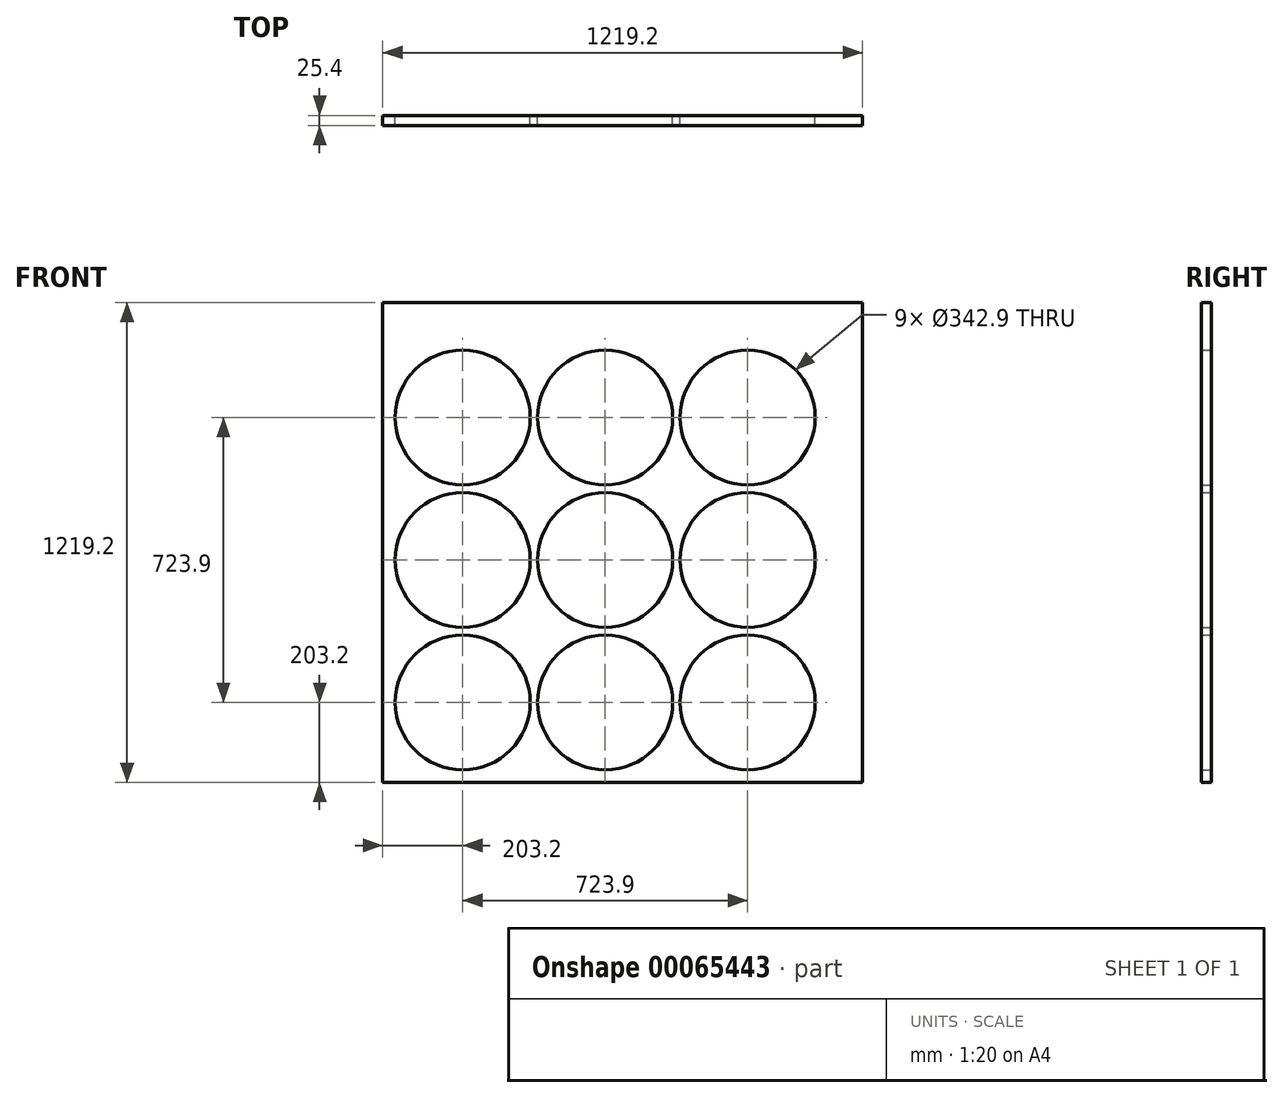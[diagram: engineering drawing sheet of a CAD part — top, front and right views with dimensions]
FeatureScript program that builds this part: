
annotation { "Feature Type Name" : "Feature", "Feature Type Description" : "" }
export const myFeature = defineFeature(function(context is Context, id is Id, definition is map)
    precondition{}
    {
        {
            var Q0;
            Q0=qCreatedBy(makeId("Front.planeOp"),FACE);
            var sketch = newSketch(context, id + "F0", { "sketchPlane" : qUnion([Q0])});
            skLineSegment(sketch, "E0", {"start": v(-609.6, 609.6) * mm, "end": v(-609.6, -609.6) * mm});
            skLineSegment(sketch, "E1", {"start": v(-609.6, -609.6) * mm, "end": v(609.6, -609.6) * mm});
            skLineSegment(sketch, "E2", {"start": v(609.6, -609.6) * mm, "end": v(609.6, 609.6) * mm});
            skLineSegment(sketch, "E3", {"start": v(609.6, 609.6) * mm, "end": v(-609.6, 609.6) * mm});
            skCircle(sketch, "E4", {"center": v(-406.4, -406.4) * mm, "radius": 171.45 * mm});
            skCircle(sketch, "E5", {"center": v(-406.4, -406.4) * mm, "radius": 69.85 * mm});
            skLineSegment(sketch, "E6", {"start": v(-387.25, -304.8) * mm, "end": v(-383, -282.22) * mm});
            skArc(sketch, "E7", {"start": v(-383, -282.22) * mm, "mid": v(-406.4, -254) * mm, "end": v(-429.8, -282.22) * mm});
            skLineSegment(sketch, "E8", {"start": v(-429.8, -282.22) * mm, "end": v(-425.55, -304.8) * mm});
            skArc(sketch, "E9", {"start": v(-425.55, -304.8) * mm, "mid": v(-406.4, -320.68) * mm, "end": v(-387.25, -304.8) * mm});
            skLineSegment(sketch, "E10", {"start": v(-440.62, -308.84) * mm, "end": v(-448.22, -287.16) * mm});
            skArc(sketch, "E11", {"start": v(-448.22, -287.16) * mm, "mid": v(-482.6, -274.42) * mm, "end": v(-488.75, -310.56) * mm});
            skLineSegment(sketch, "E12", {"start": v(-488.75, -310.56) * mm, "end": v(-473.78, -327.98) * mm});
            skArc(sketch, "E13", {"start": v(-473.78, -327.98) * mm, "mid": v(-449.26, -332.16) * mm, "end": v(-440.62, -308.84) * mm});
            skLineSegment(sketch, "E14", {"start": v(-484.82, -339.02) * mm, "end": v(-502.24, -324.05) * mm});
            skArc(sketch, "E15", {"start": v(-502.24, -324.05) * mm, "mid": v(-538.38, -330.2) * mm, "end": v(-525.64, -364.58) * mm});
            skLineSegment(sketch, "E16", {"start": v(-525.64, -364.58) * mm, "end": v(-503.96, -372.18) * mm});
            skArc(sketch, "E17", {"start": v(-503.96, -372.18) * mm, "mid": v(-480.64, -363.54) * mm, "end": v(-484.82, -339.02) * mm});
            skLineSegment(sketch, "E18", {"start": v(-508, -387.25) * mm, "end": v(-530.58, -383) * mm});
            skArc(sketch, "E19", {"start": v(-530.58, -383) * mm, "mid": v(-558.8, -406.4) * mm, "end": v(-530.58, -429.8) * mm});
            skLineSegment(sketch, "E20", {"start": v(-530.58, -429.8) * mm, "end": v(-508, -425.55) * mm});
            skArc(sketch, "E21", {"start": v(-508, -425.55) * mm, "mid": v(-492.13, -406.4) * mm, "end": v(-508, -387.25) * mm});
            skLineSegment(sketch, "E22", {"start": v(-503.96, -440.62) * mm, "end": v(-525.64, -448.22) * mm});
            skArc(sketch, "E23", {"start": v(-525.64, -448.22) * mm, "mid": v(-538.38, -482.6) * mm, "end": v(-502.24, -488.75) * mm});
            skLineSegment(sketch, "E24", {"start": v(-502.24, -488.75) * mm, "end": v(-484.82, -473.78) * mm});
            skArc(sketch, "E25", {"start": v(-484.82, -473.78) * mm, "mid": v(-480.64, -449.26) * mm, "end": v(-503.96, -440.62) * mm});
            skLineSegment(sketch, "E26", {"start": v(-473.78, -484.82) * mm, "end": v(-488.75, -502.24) * mm});
            skArc(sketch, "E27", {"start": v(-488.75, -502.24) * mm, "mid": v(-482.6, -538.38) * mm, "end": v(-448.22, -525.64) * mm});
            skLineSegment(sketch, "E28", {"start": v(-448.22, -525.64) * mm, "end": v(-440.62, -503.96) * mm});
            skArc(sketch, "E29", {"start": v(-440.62, -503.96) * mm, "mid": v(-449.26, -480.64) * mm, "end": v(-473.78, -484.82) * mm});
            skLineSegment(sketch, "E30", {"start": v(-425.55, -508) * mm, "end": v(-429.8, -530.58) * mm});
            skArc(sketch, "E31", {"start": v(-429.8, -530.58) * mm, "mid": v(-406.4, -558.8) * mm, "end": v(-383, -530.58) * mm});
            skLineSegment(sketch, "E32", {"start": v(-383, -530.58) * mm, "end": v(-387.25, -508) * mm});
            skArc(sketch, "E33", {"start": v(-387.25, -508) * mm, "mid": v(-406.4, -492.13) * mm, "end": v(-425.55, -508) * mm});
            skLineSegment(sketch, "E34", {"start": v(-372.18, -503.96) * mm, "end": v(-364.58, -525.64) * mm});
            skArc(sketch, "E35", {"start": v(-364.58, -525.64) * mm, "mid": v(-330.2, -538.38) * mm, "end": v(-324.05, -502.24) * mm});
            skLineSegment(sketch, "E36", {"start": v(-324.05, -502.24) * mm, "end": v(-339.02, -484.82) * mm});
            skArc(sketch, "E37", {"start": v(-339.02, -484.82) * mm, "mid": v(-363.54, -480.64) * mm, "end": v(-372.18, -503.96) * mm});
            skLineSegment(sketch, "E38", {"start": v(-327.98, -473.78) * mm, "end": v(-310.56, -488.75) * mm});
            skArc(sketch, "E39", {"start": v(-310.56, -488.75) * mm, "mid": v(-274.42, -482.6) * mm, "end": v(-287.16, -448.22) * mm});
            skLineSegment(sketch, "E40", {"start": v(-287.16, -448.22) * mm, "end": v(-308.84, -440.62) * mm});
            skArc(sketch, "E41", {"start": v(-308.84, -440.62) * mm, "mid": v(-332.16, -449.26) * mm, "end": v(-327.98, -473.78) * mm});
            skLineSegment(sketch, "E42", {"start": v(-304.8, -425.55) * mm, "end": v(-282.22, -429.8) * mm});
            skArc(sketch, "E43", {"start": v(-282.22, -429.8) * mm, "mid": v(-254, -406.4) * mm, "end": v(-282.22, -383) * mm});
            skLineSegment(sketch, "E44", {"start": v(-282.22, -383) * mm, "end": v(-304.8, -387.25) * mm});
            skArc(sketch, "E45", {"start": v(-304.8, -387.25) * mm, "mid": v(-320.68, -406.4) * mm, "end": v(-304.8, -425.55) * mm});
            skLineSegment(sketch, "E46", {"start": v(-308.84, -372.18) * mm, "end": v(-287.16, -364.58) * mm});
            skArc(sketch, "E47", {"start": v(-287.16, -364.58) * mm, "mid": v(-274.42, -330.2) * mm, "end": v(-310.56, -324.05) * mm});
            skLineSegment(sketch, "E48", {"start": v(-310.56, -324.05) * mm, "end": v(-327.98, -339.02) * mm});
            skArc(sketch, "E49", {"start": v(-327.98, -339.02) * mm, "mid": v(-332.16, -363.54) * mm, "end": v(-308.84, -372.18) * mm});
            skLineSegment(sketch, "E50", {"start": v(-339.02, -327.98) * mm, "end": v(-324.05, -310.56) * mm});
            skArc(sketch, "E51", {"start": v(-324.05, -310.56) * mm, "mid": v(-330.2, -274.42) * mm, "end": v(-364.58, -287.16) * mm});
            skLineSegment(sketch, "E52", {"start": v(-364.58, -287.16) * mm, "end": v(-372.18, -308.84) * mm});
            skArc(sketch, "E53", {"start": v(-372.18, -308.84) * mm, "mid": v(-363.54, -332.16) * mm, "end": v(-339.02, -327.98) * mm});
            skCircle(sketch, "E54", {"center": v(-445.73, -259.64) * mm, "radius": 7.94 * mm});
            skCircle(sketch, "E55", {"center": v(-513.84, -298.96) * mm, "radius": 7.94 * mm});
            skCircle(sketch, "E56", {"center": v(-553.16, -367.07) * mm, "radius": 7.94 * mm});
            skCircle(sketch, "E57", {"center": v(-553.16, -445.73) * mm, "radius": 7.94 * mm});
            skCircle(sketch, "E58", {"center": v(-513.84, -513.84) * mm, "radius": 7.94 * mm});
            skCircle(sketch, "E59", {"center": v(-445.73, -553.16) * mm, "radius": 7.94 * mm});
            skCircle(sketch, "E60", {"center": v(-367.07, -553.16) * mm, "radius": 7.94 * mm});
            skCircle(sketch, "E61", {"center": v(-298.96, -513.84) * mm, "radius": 7.94 * mm});
            skCircle(sketch, "E62", {"center": v(-259.64, -445.73) * mm, "radius": 7.94 * mm});
            skCircle(sketch, "E63", {"center": v(-259.64, -367.07) * mm, "radius": 7.94 * mm});
            skCircle(sketch, "E64", {"center": v(-298.96, -298.96) * mm, "radius": 7.94 * mm});
            skCircle(sketch, "E65", {"center": v(-367.07, -259.64) * mm, "radius": 7.94 * mm});
            skCircle(sketch, "E66", {"center": v(-44.45, -406.4) * mm, "radius": 171.45 * mm});
            skCircle(sketch, "E67", {"center": v(-44.45, -406.4) * mm, "radius": 69.85 * mm});
            skLineSegment(sketch, "E68", {"start": v(-25.3, -304.8) * mm, "end": v(-21.05, -282.22) * mm});
            skArc(sketch, "E69", {"start": v(-21.05, -282.22) * mm, "mid": v(-44.45, -254) * mm, "end": v(-67.85, -282.22) * mm});
            skLineSegment(sketch, "E70", {"start": v(-67.85, -282.22) * mm, "end": v(-63.6, -304.8) * mm});
            skArc(sketch, "E71", {"start": v(-63.6, -304.8) * mm, "mid": v(-44.45, -320.68) * mm, "end": v(-25.3, -304.8) * mm});
            skLineSegment(sketch, "E72", {"start": v(-78.67, -308.84) * mm, "end": v(-86.27, -287.16) * mm});
            skArc(sketch, "E73", {"start": v(-86.27, -287.16) * mm, "mid": v(-120.65, -274.42) * mm, "end": v(-126.8, -310.56) * mm});
            skLineSegment(sketch, "E74", {"start": v(-126.8, -310.56) * mm, "end": v(-111.83, -327.98) * mm});
            skArc(sketch, "E75", {"start": v(-111.83, -327.98) * mm, "mid": v(-87.31, -332.16) * mm, "end": v(-78.67, -308.84) * mm});
            skLineSegment(sketch, "E76", {"start": v(-122.87, -339.02) * mm, "end": v(-140.3, -324.05) * mm});
            skArc(sketch, "E77", {"start": v(-140.3, -324.05) * mm, "mid": v(-176.43, -330.2) * mm, "end": v(-163.7, -364.58) * mm});
            skLineSegment(sketch, "E78", {"start": v(-163.7, -364.58) * mm, "end": v(-142.01, -372.18) * mm});
            skArc(sketch, "E79", {"start": v(-142.01, -372.18) * mm, "mid": v(-118.7, -363.54) * mm, "end": v(-122.87, -339.02) * mm});
            skLineSegment(sketch, "E80", {"start": v(-146.05, -387.25) * mm, "end": v(-168.63, -383) * mm});
            skArc(sketch, "E81", {"start": v(-168.63, -383) * mm, "mid": v(-196.85, -406.4) * mm, "end": v(-168.63, -429.8) * mm});
            skLineSegment(sketch, "E82", {"start": v(-168.63, -429.8) * mm, "end": v(-146.05, -425.55) * mm});
            skArc(sketch, "E83", {"start": v(-146.05, -425.55) * mm, "mid": v(-130.18, -406.4) * mm, "end": v(-146.05, -387.25) * mm});
            skLineSegment(sketch, "E84", {"start": v(-142.01, -440.62) * mm, "end": v(-163.7, -448.22) * mm});
            skArc(sketch, "E85", {"start": v(-163.7, -448.22) * mm, "mid": v(-176.43, -482.6) * mm, "end": v(-140.3, -488.75) * mm});
            skLineSegment(sketch, "E86", {"start": v(-140.3, -488.75) * mm, "end": v(-122.87, -473.78) * mm});
            skArc(sketch, "E87", {"start": v(-122.87, -473.78) * mm, "mid": v(-118.7, -449.26) * mm, "end": v(-142.01, -440.62) * mm});
            skLineSegment(sketch, "E88", {"start": v(-111.83, -484.82) * mm, "end": v(-126.8, -502.24) * mm});
            skArc(sketch, "E89", {"start": v(-126.8, -502.24) * mm, "mid": v(-120.65, -538.38) * mm, "end": v(-86.27, -525.64) * mm});
            skLineSegment(sketch, "E90", {"start": v(-86.27, -525.64) * mm, "end": v(-78.67, -503.96) * mm});
            skArc(sketch, "E91", {"start": v(-78.67, -503.96) * mm, "mid": v(-87.31, -480.64) * mm, "end": v(-111.83, -484.82) * mm});
            skLineSegment(sketch, "E92", {"start": v(-63.6, -508) * mm, "end": v(-67.85, -530.58) * mm});
            skArc(sketch, "E93", {"start": v(-67.85, -530.58) * mm, "mid": v(-44.45, -558.8) * mm, "end": v(-21.05, -530.58) * mm});
            skLineSegment(sketch, "E94", {"start": v(-21.05, -530.58) * mm, "end": v(-25.3, -508) * mm});
            skArc(sketch, "E95", {"start": v(-25.3, -508) * mm, "mid": v(-44.45, -492.13) * mm, "end": v(-63.6, -508) * mm});
            skLineSegment(sketch, "E96", {"start": v(-10.23, -503.96) * mm, "end": v(-2.63, -525.64) * mm});
            skArc(sketch, "E97", {"start": v(-2.63, -525.64) * mm, "mid": v(31.75, -538.38) * mm, "end": v(37.9, -502.24) * mm});
            skLineSegment(sketch, "E98", {"start": v(37.9, -502.24) * mm, "end": v(22.93, -484.82) * mm});
            skArc(sketch, "E99", {"start": v(22.93, -484.82) * mm, "mid": v(-1.59, -480.64) * mm, "end": v(-10.23, -503.96) * mm});
            skLineSegment(sketch, "E100", {"start": v(33.97, -473.78) * mm, "end": v(51.4, -488.75) * mm});
            skArc(sketch, "E101", {"start": v(51.4, -488.75) * mm, "mid": v(87.53, -482.6) * mm, "end": v(74.8, -448.22) * mm});
            skLineSegment(sketch, "E102", {"start": v(74.8, -448.22) * mm, "end": v(53.11, -440.62) * mm});
            skArc(sketch, "E103", {"start": v(53.11, -440.62) * mm, "mid": v(29.8, -449.26) * mm, "end": v(33.97, -473.78) * mm});
            skLineSegment(sketch, "E104", {"start": v(57.15, -425.55) * mm, "end": v(79.73, -429.8) * mm});
            skArc(sketch, "E105", {"start": v(79.73, -429.8) * mm, "mid": v(107.95, -406.4) * mm, "end": v(79.73, -383) * mm});
            skLineSegment(sketch, "E106", {"start": v(79.73, -383) * mm, "end": v(57.15, -387.25) * mm});
            skArc(sketch, "E107", {"start": v(57.15, -387.25) * mm, "mid": v(41.27, -406.4) * mm, "end": v(57.15, -425.55) * mm});
            skLineSegment(sketch, "E108", {"start": v(53.11, -372.18) * mm, "end": v(74.8, -364.58) * mm});
            skArc(sketch, "E109", {"start": v(74.8, -364.58) * mm, "mid": v(87.53, -330.2) * mm, "end": v(51.4, -324.05) * mm});
            skLineSegment(sketch, "E110", {"start": v(51.4, -324.05) * mm, "end": v(33.97, -339.02) * mm});
            skArc(sketch, "E111", {"start": v(33.97, -339.02) * mm, "mid": v(29.8, -363.54) * mm, "end": v(53.11, -372.18) * mm});
            skLineSegment(sketch, "E112", {"start": v(22.93, -327.98) * mm, "end": v(37.9, -310.56) * mm});
            skArc(sketch, "E113", {"start": v(37.9, -310.56) * mm, "mid": v(31.75, -274.42) * mm, "end": v(-2.63, -287.16) * mm});
            skLineSegment(sketch, "E114", {"start": v(-2.63, -287.16) * mm, "end": v(-10.23, -308.84) * mm});
            skArc(sketch, "E115", {"start": v(-10.23, -308.84) * mm, "mid": v(-1.59, -332.16) * mm, "end": v(22.93, -327.98) * mm});
            skCircle(sketch, "E116", {"center": v(-83.78, -259.64) * mm, "radius": 7.94 * mm});
            skCircle(sketch, "E117", {"center": v(-151.89, -298.96) * mm, "radius": 7.94 * mm});
            skCircle(sketch, "E118", {"center": v(-191.21, -367.07) * mm, "radius": 7.94 * mm});
            skCircle(sketch, "E119", {"center": v(-191.21, -445.73) * mm, "radius": 7.94 * mm});
            skCircle(sketch, "E120", {"center": v(-151.89, -513.84) * mm, "radius": 7.94 * mm});
            skCircle(sketch, "E121", {"center": v(-83.78, -553.16) * mm, "radius": 7.94 * mm});
            skCircle(sketch, "E122", {"center": v(-5.12, -553.16) * mm, "radius": 7.94 * mm});
            skCircle(sketch, "E123", {"center": v(62.99, -513.84) * mm, "radius": 7.94 * mm});
            skCircle(sketch, "E124", {"center": v(102.31, -445.73) * mm, "radius": 7.94 * mm});
            skCircle(sketch, "E125", {"center": v(102.31, -367.07) * mm, "radius": 7.94 * mm});
            skCircle(sketch, "E126", {"center": v(62.99, -298.96) * mm, "radius": 7.94 * mm});
            skCircle(sketch, "E127", {"center": v(-5.12, -259.64) * mm, "radius": 7.94 * mm});
            skCircle(sketch, "E128", {"center": v(317.5, -406.4) * mm, "radius": 171.45 * mm});
            skCircle(sketch, "E129", {"center": v(317.5, -406.4) * mm, "radius": 69.85 * mm});
            skLineSegment(sketch, "E130", {"start": v(336.65, -304.8) * mm, "end": v(340.9, -282.22) * mm});
            skArc(sketch, "E131", {"start": v(340.9, -282.22) * mm, "mid": v(317.5, -254) * mm, "end": v(294.1, -282.22) * mm});
            skLineSegment(sketch, "E132", {"start": v(294.1, -282.22) * mm, "end": v(298.35, -304.8) * mm});
            skArc(sketch, "E133", {"start": v(298.35, -304.8) * mm, "mid": v(317.5, -320.68) * mm, "end": v(336.65, -304.8) * mm});
            skLineSegment(sketch, "E134", {"start": v(283.28, -308.84) * mm, "end": v(275.68, -287.16) * mm});
            skArc(sketch, "E135", {"start": v(275.68, -287.16) * mm, "mid": v(241.3, -274.42) * mm, "end": v(235.15, -310.56) * mm});
            skLineSegment(sketch, "E136", {"start": v(235.15, -310.56) * mm, "end": v(250.12, -327.98) * mm});
            skArc(sketch, "E137", {"start": v(250.12, -327.98) * mm, "mid": v(274.64, -332.16) * mm, "end": v(283.28, -308.84) * mm});
            skLineSegment(sketch, "E138", {"start": v(239.08, -339.02) * mm, "end": v(221.66, -324.05) * mm});
            skArc(sketch, "E139", {"start": v(221.66, -324.05) * mm, "mid": v(185.52, -330.2) * mm, "end": v(198.26, -364.58) * mm});
            skLineSegment(sketch, "E140", {"start": v(198.26, -364.58) * mm, "end": v(219.94, -372.18) * mm});
            skArc(sketch, "E141", {"start": v(219.94, -372.18) * mm, "mid": v(243.26, -363.54) * mm, "end": v(239.08, -339.02) * mm});
            skLineSegment(sketch, "E142", {"start": v(215.9, -387.25) * mm, "end": v(193.32, -383) * mm});
            skArc(sketch, "E143", {"start": v(193.32, -383) * mm, "mid": v(165.1, -406.4) * mm, "end": v(193.32, -429.8) * mm});
            skLineSegment(sketch, "E144", {"start": v(193.32, -429.8) * mm, "end": v(215.9, -425.55) * mm});
            skArc(sketch, "E145", {"start": v(215.9, -425.55) * mm, "mid": v(231.77, -406.4) * mm, "end": v(215.9, -387.25) * mm});
            skLineSegment(sketch, "E146", {"start": v(219.94, -440.62) * mm, "end": v(198.26, -448.22) * mm});
            skArc(sketch, "E147", {"start": v(198.26, -448.22) * mm, "mid": v(185.52, -482.6) * mm, "end": v(221.66, -488.75) * mm});
            skLineSegment(sketch, "E148", {"start": v(221.66, -488.75) * mm, "end": v(239.08, -473.78) * mm});
            skArc(sketch, "E149", {"start": v(239.08, -473.78) * mm, "mid": v(243.26, -449.26) * mm, "end": v(219.94, -440.62) * mm});
            skLineSegment(sketch, "E150", {"start": v(250.12, -484.82) * mm, "end": v(235.15, -502.24) * mm});
            skArc(sketch, "E151", {"start": v(235.15, -502.24) * mm, "mid": v(241.3, -538.38) * mm, "end": v(275.68, -525.64) * mm});
            skLineSegment(sketch, "E152", {"start": v(275.68, -525.64) * mm, "end": v(283.28, -503.96) * mm});
            skArc(sketch, "E153", {"start": v(283.28, -503.96) * mm, "mid": v(274.64, -480.64) * mm, "end": v(250.12, -484.82) * mm});
            skLineSegment(sketch, "E154", {"start": v(298.35, -508) * mm, "end": v(294.1, -530.58) * mm});
            skArc(sketch, "E155", {"start": v(294.1, -530.58) * mm, "mid": v(317.5, -558.8) * mm, "end": v(340.9, -530.58) * mm});
            skLineSegment(sketch, "E156", {"start": v(340.9, -530.58) * mm, "end": v(336.65, -508) * mm});
            skArc(sketch, "E157", {"start": v(336.65, -508) * mm, "mid": v(317.5, -492.13) * mm, "end": v(298.35, -508) * mm});
            skLineSegment(sketch, "E158", {"start": v(351.72, -503.96) * mm, "end": v(359.32, -525.64) * mm});
            skArc(sketch, "E159", {"start": v(359.32, -525.64) * mm, "mid": v(393.7, -538.38) * mm, "end": v(399.85, -502.24) * mm});
            skLineSegment(sketch, "E160", {"start": v(399.85, -502.24) * mm, "end": v(384.88, -484.82) * mm});
            skArc(sketch, "E161", {"start": v(384.88, -484.82) * mm, "mid": v(360.36, -480.64) * mm, "end": v(351.72, -503.96) * mm});
            skLineSegment(sketch, "E162", {"start": v(395.92, -473.78) * mm, "end": v(413.34, -488.75) * mm});
            skArc(sketch, "E163", {"start": v(413.34, -488.75) * mm, "mid": v(449.48, -482.6) * mm, "end": v(436.74, -448.22) * mm});
            skLineSegment(sketch, "E164", {"start": v(436.74, -448.22) * mm, "end": v(415.06, -440.62) * mm});
            skArc(sketch, "E165", {"start": v(415.06, -440.62) * mm, "mid": v(391.74, -449.26) * mm, "end": v(395.92, -473.78) * mm});
            skLineSegment(sketch, "E166", {"start": v(419.1, -425.55) * mm, "end": v(441.68, -429.8) * mm});
            skArc(sketch, "E167", {"start": v(441.68, -429.8) * mm, "mid": v(469.9, -406.4) * mm, "end": v(441.68, -383) * mm});
            skLineSegment(sketch, "E168", {"start": v(441.68, -383) * mm, "end": v(419.1, -387.25) * mm});
            skArc(sketch, "E169", {"start": v(419.1, -387.25) * mm, "mid": v(403.23, -406.4) * mm, "end": v(419.1, -425.55) * mm});
            skLineSegment(sketch, "E170", {"start": v(415.06, -372.18) * mm, "end": v(436.74, -364.58) * mm});
            skArc(sketch, "E171", {"start": v(436.74, -364.58) * mm, "mid": v(449.48, -330.2) * mm, "end": v(413.34, -324.05) * mm});
            skLineSegment(sketch, "E172", {"start": v(413.34, -324.05) * mm, "end": v(395.92, -339.02) * mm});
            skArc(sketch, "E173", {"start": v(395.92, -339.02) * mm, "mid": v(391.74, -363.54) * mm, "end": v(415.06, -372.18) * mm});
            skLineSegment(sketch, "E174", {"start": v(384.88, -327.98) * mm, "end": v(399.85, -310.56) * mm});
            skArc(sketch, "E175", {"start": v(399.85, -310.56) * mm, "mid": v(393.7, -274.42) * mm, "end": v(359.32, -287.16) * mm});
            skLineSegment(sketch, "E176", {"start": v(359.32, -287.16) * mm, "end": v(351.72, -308.84) * mm});
            skArc(sketch, "E177", {"start": v(351.72, -308.84) * mm, "mid": v(360.36, -332.16) * mm, "end": v(384.88, -327.98) * mm});
            skCircle(sketch, "E178", {"center": v(278.17, -259.64) * mm, "radius": 7.94 * mm});
            skCircle(sketch, "E179", {"center": v(210.06, -298.96) * mm, "radius": 7.94 * mm});
            skCircle(sketch, "E180", {"center": v(170.74, -367.07) * mm, "radius": 7.94 * mm});
            skCircle(sketch, "E181", {"center": v(170.74, -445.73) * mm, "radius": 7.94 * mm});
            skCircle(sketch, "E182", {"center": v(210.06, -513.84) * mm, "radius": 7.94 * mm});
            skCircle(sketch, "E183", {"center": v(278.17, -553.16) * mm, "radius": 7.94 * mm});
            skCircle(sketch, "E184", {"center": v(356.83, -553.16) * mm, "radius": 7.94 * mm});
            skCircle(sketch, "E185", {"center": v(424.94, -513.84) * mm, "radius": 7.94 * mm});
            skCircle(sketch, "E186", {"center": v(464.26, -445.73) * mm, "radius": 7.94 * mm});
            skCircle(sketch, "E187", {"center": v(464.26, -367.07) * mm, "radius": 7.94 * mm});
            skCircle(sketch, "E188", {"center": v(424.94, -298.96) * mm, "radius": 7.94 * mm});
            skCircle(sketch, "E189", {"center": v(356.83, -259.64) * mm, "radius": 7.94 * mm});
            skCircle(sketch, "E190", {"center": v(-44.45, -44.45) * mm, "radius": 171.45 * mm});
            skCircle(sketch, "E191", {"center": v(-44.45, -44.45) * mm, "radius": 69.85 * mm});
            skLineSegment(sketch, "E192", {"start": v(-25.3, 57.15) * mm, "end": v(-21.05, 79.73) * mm});
            skArc(sketch, "E193", {"start": v(-21.05, 79.73) * mm, "mid": v(-44.45, 107.95) * mm, "end": v(-67.85, 79.73) * mm});
            skLineSegment(sketch, "E194", {"start": v(-67.85, 79.73) * mm, "end": v(-63.6, 57.15) * mm});
            skArc(sketch, "E195", {"start": v(-63.6, 57.15) * mm, "mid": v(-44.45, 41.27) * mm, "end": v(-25.3, 57.15) * mm});
            skLineSegment(sketch, "E196", {"start": v(-78.67, 53.11) * mm, "end": v(-86.27, 74.8) * mm});
            skArc(sketch, "E197", {"start": v(-86.27, 74.8) * mm, "mid": v(-120.65, 87.53) * mm, "end": v(-126.8, 51.4) * mm});
            skLineSegment(sketch, "E198", {"start": v(-126.8, 51.4) * mm, "end": v(-111.83, 33.97) * mm});
            skArc(sketch, "E199", {"start": v(-111.83, 33.97) * mm, "mid": v(-87.31, 29.8) * mm, "end": v(-78.67, 53.11) * mm});
            skLineSegment(sketch, "E200", {"start": v(-122.87, 22.93) * mm, "end": v(-140.3, 37.9) * mm});
            skArc(sketch, "E201", {"start": v(-140.3, 37.9) * mm, "mid": v(-176.43, 31.75) * mm, "end": v(-163.7, -2.63) * mm});
            skLineSegment(sketch, "E202", {"start": v(-163.7, -2.63) * mm, "end": v(-142.01, -10.23) * mm});
            skArc(sketch, "E203", {"start": v(-142.01, -10.23) * mm, "mid": v(-118.7, -1.59) * mm, "end": v(-122.87, 22.93) * mm});
            skLineSegment(sketch, "E204", {"start": v(-146.05, -25.3) * mm, "end": v(-168.63, -21.05) * mm});
            skArc(sketch, "E205", {"start": v(-168.63, -21.05) * mm, "mid": v(-196.85, -44.45) * mm, "end": v(-168.63, -67.85) * mm});
            skLineSegment(sketch, "E206", {"start": v(-168.63, -67.85) * mm, "end": v(-146.05, -63.6) * mm});
            skArc(sketch, "E207", {"start": v(-146.05, -63.6) * mm, "mid": v(-130.18, -44.45) * mm, "end": v(-146.05, -25.3) * mm});
            skLineSegment(sketch, "E208", {"start": v(-142.01, -78.67) * mm, "end": v(-163.7, -86.27) * mm});
            skArc(sketch, "E209", {"start": v(-163.7, -86.27) * mm, "mid": v(-176.43, -120.65) * mm, "end": v(-140.3, -126.8) * mm});
            skLineSegment(sketch, "E210", {"start": v(-140.3, -126.8) * mm, "end": v(-122.87, -111.83) * mm});
            skArc(sketch, "E211", {"start": v(-122.87, -111.83) * mm, "mid": v(-118.7, -87.31) * mm, "end": v(-142.01, -78.67) * mm});
            skLineSegment(sketch, "E212", {"start": v(-111.83, -122.87) * mm, "end": v(-126.8, -140.3) * mm});
            skArc(sketch, "E213", {"start": v(-126.8, -140.3) * mm, "mid": v(-120.65, -176.43) * mm, "end": v(-86.27, -163.7) * mm});
            skLineSegment(sketch, "E214", {"start": v(-86.27, -163.7) * mm, "end": v(-78.67, -142.01) * mm});
            skArc(sketch, "E215", {"start": v(-78.67, -142.01) * mm, "mid": v(-87.31, -118.7) * mm, "end": v(-111.83, -122.87) * mm});
            skLineSegment(sketch, "E216", {"start": v(-63.6, -146.05) * mm, "end": v(-67.85, -168.63) * mm});
            skArc(sketch, "E217", {"start": v(-67.85, -168.63) * mm, "mid": v(-44.45, -196.85) * mm, "end": v(-21.05, -168.63) * mm});
            skLineSegment(sketch, "E218", {"start": v(-21.05, -168.63) * mm, "end": v(-25.3, -146.05) * mm});
            skArc(sketch, "E219", {"start": v(-25.3, -146.05) * mm, "mid": v(-44.45, -130.18) * mm, "end": v(-63.6, -146.05) * mm});
            skLineSegment(sketch, "E220", {"start": v(-10.23, -142.01) * mm, "end": v(-2.63, -163.7) * mm});
            skArc(sketch, "E221", {"start": v(-2.63, -163.7) * mm, "mid": v(31.75, -176.43) * mm, "end": v(37.9, -140.3) * mm});
            skLineSegment(sketch, "E222", {"start": v(37.9, -140.3) * mm, "end": v(22.93, -122.87) * mm});
            skArc(sketch, "E223", {"start": v(22.93, -122.87) * mm, "mid": v(-1.59, -118.7) * mm, "end": v(-10.23, -142.01) * mm});
            skLineSegment(sketch, "E224", {"start": v(33.97, -111.83) * mm, "end": v(51.4, -126.8) * mm});
            skArc(sketch, "E225", {"start": v(51.4, -126.8) * mm, "mid": v(87.53, -120.65) * mm, "end": v(74.8, -86.27) * mm});
            skLineSegment(sketch, "E226", {"start": v(74.8, -86.27) * mm, "end": v(53.11, -78.67) * mm});
            skArc(sketch, "E227", {"start": v(53.11, -78.67) * mm, "mid": v(29.8, -87.31) * mm, "end": v(33.97, -111.83) * mm});
            skLineSegment(sketch, "E228", {"start": v(57.15, -63.6) * mm, "end": v(79.73, -67.85) * mm});
            skArc(sketch, "E229", {"start": v(79.73, -67.85) * mm, "mid": v(107.95, -44.45) * mm, "end": v(79.73, -21.05) * mm});
            skLineSegment(sketch, "E230", {"start": v(79.73, -21.05) * mm, "end": v(57.15, -25.3) * mm});
            skArc(sketch, "E231", {"start": v(57.15, -25.3) * mm, "mid": v(41.27, -44.45) * mm, "end": v(57.15, -63.6) * mm});
            skLineSegment(sketch, "E232", {"start": v(53.11, -10.23) * mm, "end": v(74.8, -2.63) * mm});
            skArc(sketch, "E233", {"start": v(74.8, -2.63) * mm, "mid": v(87.53, 31.75) * mm, "end": v(51.4, 37.9) * mm});
            skLineSegment(sketch, "E234", {"start": v(51.4, 37.9) * mm, "end": v(33.97, 22.93) * mm});
            skArc(sketch, "E235", {"start": v(33.97, 22.93) * mm, "mid": v(29.8, -1.59) * mm, "end": v(53.11, -10.23) * mm});
            skLineSegment(sketch, "E236", {"start": v(22.93, 33.97) * mm, "end": v(37.9, 51.4) * mm});
            skArc(sketch, "E237", {"start": v(37.9, 51.4) * mm, "mid": v(31.75, 87.53) * mm, "end": v(-2.63, 74.8) * mm});
            skLineSegment(sketch, "E238", {"start": v(-2.63, 74.8) * mm, "end": v(-10.23, 53.11) * mm});
            skArc(sketch, "E239", {"start": v(-10.23, 53.11) * mm, "mid": v(-1.59, 29.8) * mm, "end": v(22.93, 33.97) * mm});
            skCircle(sketch, "E240", {"center": v(-83.78, 102.31) * mm, "radius": 7.94 * mm});
            skCircle(sketch, "E241", {"center": v(-151.89, 62.99) * mm, "radius": 7.94 * mm});
            skCircle(sketch, "E242", {"center": v(-191.21, -5.12) * mm, "radius": 7.94 * mm});
            skCircle(sketch, "E243", {"center": v(-191.21, -83.78) * mm, "radius": 7.94 * mm});
            skCircle(sketch, "E244", {"center": v(-151.89, -151.89) * mm, "radius": 7.94 * mm});
            skCircle(sketch, "E245", {"center": v(-83.78, -191.21) * mm, "radius": 7.94 * mm});
            skCircle(sketch, "E246", {"center": v(-5.12, -191.21) * mm, "radius": 7.94 * mm});
            skCircle(sketch, "E247", {"center": v(62.99, -151.89) * mm, "radius": 7.94 * mm});
            skCircle(sketch, "E248", {"center": v(102.31, -83.78) * mm, "radius": 7.94 * mm});
            skCircle(sketch, "E249", {"center": v(102.31, -5.12) * mm, "radius": 7.94 * mm});
            skCircle(sketch, "E250", {"center": v(62.99, 62.99) * mm, "radius": 7.94 * mm});
            skCircle(sketch, "E251", {"center": v(-5.12, 102.31) * mm, "radius": 7.94 * mm});
            skCircle(sketch, "E252", {"center": v(317.5, -44.45) * mm, "radius": 171.45 * mm});
            skCircle(sketch, "E253", {"center": v(317.5, -44.45) * mm, "radius": 69.85 * mm});
            skLineSegment(sketch, "E254", {"start": v(336.65, 57.15) * mm, "end": v(340.9, 79.73) * mm});
            skArc(sketch, "E255", {"start": v(340.9, 79.73) * mm, "mid": v(317.5, 107.95) * mm, "end": v(294.1, 79.73) * mm});
            skLineSegment(sketch, "E256", {"start": v(294.1, 79.73) * mm, "end": v(298.35, 57.15) * mm});
            skArc(sketch, "E257", {"start": v(298.35, 57.15) * mm, "mid": v(317.5, 41.27) * mm, "end": v(336.65, 57.15) * mm});
            skLineSegment(sketch, "E258", {"start": v(283.28, 53.11) * mm, "end": v(275.68, 74.8) * mm});
            skArc(sketch, "E259", {"start": v(275.68, 74.8) * mm, "mid": v(241.3, 87.53) * mm, "end": v(235.15, 51.4) * mm});
            skLineSegment(sketch, "E260", {"start": v(235.15, 51.4) * mm, "end": v(250.12, 33.97) * mm});
            skArc(sketch, "E261", {"start": v(250.12, 33.97) * mm, "mid": v(274.64, 29.8) * mm, "end": v(283.28, 53.11) * mm});
            skLineSegment(sketch, "E262", {"start": v(239.08, 22.93) * mm, "end": v(221.66, 37.9) * mm});
            skArc(sketch, "E263", {"start": v(221.66, 37.9) * mm, "mid": v(185.52, 31.75) * mm, "end": v(198.26, -2.63) * mm});
            skLineSegment(sketch, "E264", {"start": v(198.26, -2.63) * mm, "end": v(219.94, -10.23) * mm});
            skArc(sketch, "E265", {"start": v(219.94, -10.23) * mm, "mid": v(243.26, -1.59) * mm, "end": v(239.08, 22.93) * mm});
            skLineSegment(sketch, "E266", {"start": v(215.9, -25.3) * mm, "end": v(193.32, -21.05) * mm});
            skArc(sketch, "E267", {"start": v(193.32, -21.05) * mm, "mid": v(165.1, -44.45) * mm, "end": v(193.32, -67.85) * mm});
            skLineSegment(sketch, "E268", {"start": v(193.32, -67.85) * mm, "end": v(215.9, -63.6) * mm});
            skArc(sketch, "E269", {"start": v(215.9, -63.6) * mm, "mid": v(231.77, -44.45) * mm, "end": v(215.9, -25.3) * mm});
            skLineSegment(sketch, "E270", {"start": v(219.94, -78.67) * mm, "end": v(198.26, -86.27) * mm});
            skArc(sketch, "E271", {"start": v(198.26, -86.27) * mm, "mid": v(185.52, -120.65) * mm, "end": v(221.66, -126.8) * mm});
            skLineSegment(sketch, "E272", {"start": v(221.66, -126.8) * mm, "end": v(239.08, -111.83) * mm});
            skArc(sketch, "E273", {"start": v(239.08, -111.83) * mm, "mid": v(243.26, -87.31) * mm, "end": v(219.94, -78.67) * mm});
            skLineSegment(sketch, "E274", {"start": v(250.12, -122.87) * mm, "end": v(235.15, -140.3) * mm});
            skArc(sketch, "E275", {"start": v(235.15, -140.3) * mm, "mid": v(241.3, -176.43) * mm, "end": v(275.68, -163.7) * mm});
            skLineSegment(sketch, "E276", {"start": v(275.68, -163.7) * mm, "end": v(283.28, -142.01) * mm});
            skArc(sketch, "E277", {"start": v(283.28, -142.01) * mm, "mid": v(274.64, -118.7) * mm, "end": v(250.12, -122.87) * mm});
            skLineSegment(sketch, "E278", {"start": v(298.35, -146.05) * mm, "end": v(294.1, -168.63) * mm});
            skArc(sketch, "E279", {"start": v(294.1, -168.63) * mm, "mid": v(317.5, -196.85) * mm, "end": v(340.9, -168.63) * mm});
            skLineSegment(sketch, "E280", {"start": v(340.9, -168.63) * mm, "end": v(336.65, -146.05) * mm});
            skArc(sketch, "E281", {"start": v(336.65, -146.05) * mm, "mid": v(317.5, -130.18) * mm, "end": v(298.35, -146.05) * mm});
            skLineSegment(sketch, "E282", {"start": v(351.72, -142.01) * mm, "end": v(359.32, -163.7) * mm});
            skArc(sketch, "E283", {"start": v(359.32, -163.7) * mm, "mid": v(393.7, -176.43) * mm, "end": v(399.85, -140.3) * mm});
            skLineSegment(sketch, "E284", {"start": v(399.85, -140.3) * mm, "end": v(384.88, -122.87) * mm});
            skArc(sketch, "E285", {"start": v(384.88, -122.87) * mm, "mid": v(360.36, -118.7) * mm, "end": v(351.72, -142.01) * mm});
            skLineSegment(sketch, "E286", {"start": v(395.92, -111.83) * mm, "end": v(413.34, -126.8) * mm});
            skArc(sketch, "E287", {"start": v(413.34, -126.8) * mm, "mid": v(449.48, -120.65) * mm, "end": v(436.74, -86.27) * mm});
            skLineSegment(sketch, "E288", {"start": v(436.74, -86.27) * mm, "end": v(415.06, -78.67) * mm});
            skArc(sketch, "E289", {"start": v(415.06, -78.67) * mm, "mid": v(391.74, -87.31) * mm, "end": v(395.92, -111.83) * mm});
            skLineSegment(sketch, "E290", {"start": v(419.1, -63.6) * mm, "end": v(441.68, -67.85) * mm});
            skArc(sketch, "E291", {"start": v(441.68, -67.85) * mm, "mid": v(469.9, -44.45) * mm, "end": v(441.68, -21.05) * mm});
            skLineSegment(sketch, "E292", {"start": v(441.68, -21.05) * mm, "end": v(419.1, -25.3) * mm});
            skArc(sketch, "E293", {"start": v(419.1, -25.3) * mm, "mid": v(403.23, -44.45) * mm, "end": v(419.1, -63.6) * mm});
            skLineSegment(sketch, "E294", {"start": v(415.06, -10.23) * mm, "end": v(436.74, -2.63) * mm});
            skArc(sketch, "E295", {"start": v(436.74, -2.63) * mm, "mid": v(449.48, 31.75) * mm, "end": v(413.34, 37.9) * mm});
            skLineSegment(sketch, "E296", {"start": v(413.34, 37.9) * mm, "end": v(395.92, 22.93) * mm});
            skArc(sketch, "E297", {"start": v(395.92, 22.93) * mm, "mid": v(391.74, -1.59) * mm, "end": v(415.06, -10.23) * mm});
            skLineSegment(sketch, "E298", {"start": v(384.88, 33.97) * mm, "end": v(399.85, 51.4) * mm});
            skArc(sketch, "E299", {"start": v(399.85, 51.4) * mm, "mid": v(393.7, 87.53) * mm, "end": v(359.32, 74.8) * mm});
            skLineSegment(sketch, "E300", {"start": v(359.32, 74.8) * mm, "end": v(351.72, 53.11) * mm});
            skArc(sketch, "E301", {"start": v(351.72, 53.11) * mm, "mid": v(360.36, 29.8) * mm, "end": v(384.88, 33.97) * mm});
            skCircle(sketch, "E302", {"center": v(278.17, 102.31) * mm, "radius": 7.94 * mm});
            skCircle(sketch, "E303", {"center": v(210.06, 62.99) * mm, "radius": 7.94 * mm});
            skCircle(sketch, "E304", {"center": v(170.74, -5.12) * mm, "radius": 7.94 * mm});
            skCircle(sketch, "E305", {"center": v(170.74, -83.78) * mm, "radius": 7.94 * mm});
            skCircle(sketch, "E306", {"center": v(210.06, -151.89) * mm, "radius": 7.94 * mm});
            skCircle(sketch, "E307", {"center": v(278.17, -191.21) * mm, "radius": 7.94 * mm});
            skCircle(sketch, "E308", {"center": v(356.83, -191.21) * mm, "radius": 7.94 * mm});
            skCircle(sketch, "E309", {"center": v(424.94, -151.89) * mm, "radius": 7.94 * mm});
            skCircle(sketch, "E310", {"center": v(464.26, -83.78) * mm, "radius": 7.94 * mm});
            skCircle(sketch, "E311", {"center": v(464.26, -5.12) * mm, "radius": 7.94 * mm});
            skCircle(sketch, "E312", {"center": v(424.94, 62.99) * mm, "radius": 7.94 * mm});
            skCircle(sketch, "E313", {"center": v(356.83, 102.31) * mm, "radius": 7.94 * mm});
            skCircle(sketch, "E314", {"center": v(-406.4, -44.45) * mm, "radius": 171.45 * mm});
            skCircle(sketch, "E315", {"center": v(-406.4, -44.45) * mm, "radius": 69.85 * mm});
            skLineSegment(sketch, "E316", {"start": v(-387.25, 57.15) * mm, "end": v(-383, 79.73) * mm});
            skArc(sketch, "E317", {"start": v(-383, 79.73) * mm, "mid": v(-406.4, 107.95) * mm, "end": v(-429.8, 79.73) * mm});
            skLineSegment(sketch, "E318", {"start": v(-429.8, 79.73) * mm, "end": v(-425.55, 57.15) * mm});
            skArc(sketch, "E319", {"start": v(-425.55, 57.15) * mm, "mid": v(-406.4, 41.27) * mm, "end": v(-387.25, 57.15) * mm});
            skLineSegment(sketch, "E320", {"start": v(-440.62, 53.11) * mm, "end": v(-448.22, 74.8) * mm});
            skArc(sketch, "E321", {"start": v(-448.22, 74.8) * mm, "mid": v(-482.6, 87.53) * mm, "end": v(-488.75, 51.4) * mm});
            skLineSegment(sketch, "E322", {"start": v(-488.75, 51.4) * mm, "end": v(-473.78, 33.97) * mm});
            skArc(sketch, "E323", {"start": v(-473.78, 33.97) * mm, "mid": v(-449.26, 29.8) * mm, "end": v(-440.62, 53.11) * mm});
            skLineSegment(sketch, "E324", {"start": v(-484.82, 22.93) * mm, "end": v(-502.24, 37.9) * mm});
            skArc(sketch, "E325", {"start": v(-502.24, 37.9) * mm, "mid": v(-538.38, 31.75) * mm, "end": v(-525.64, -2.63) * mm});
            skLineSegment(sketch, "E326", {"start": v(-525.64, -2.63) * mm, "end": v(-503.96, -10.23) * mm});
            skArc(sketch, "E327", {"start": v(-503.96, -10.23) * mm, "mid": v(-480.64, -1.59) * mm, "end": v(-484.82, 22.93) * mm});
            skLineSegment(sketch, "E328", {"start": v(-508, -25.3) * mm, "end": v(-530.58, -21.05) * mm});
            skArc(sketch, "E329", {"start": v(-530.58, -21.05) * mm, "mid": v(-558.8, -44.45) * mm, "end": v(-530.58, -67.85) * mm});
            skLineSegment(sketch, "E330", {"start": v(-530.58, -67.85) * mm, "end": v(-508, -63.6) * mm});
            skArc(sketch, "E331", {"start": v(-508, -63.6) * mm, "mid": v(-492.13, -44.45) * mm, "end": v(-508, -25.3) * mm});
            skLineSegment(sketch, "E332", {"start": v(-503.96, -78.67) * mm, "end": v(-525.64, -86.27) * mm});
            skArc(sketch, "E333", {"start": v(-525.64, -86.27) * mm, "mid": v(-538.38, -120.65) * mm, "end": v(-502.24, -126.8) * mm});
            skLineSegment(sketch, "E334", {"start": v(-502.24, -126.8) * mm, "end": v(-484.82, -111.83) * mm});
            skArc(sketch, "E335", {"start": v(-484.82, -111.83) * mm, "mid": v(-480.64, -87.31) * mm, "end": v(-503.96, -78.67) * mm});
            skLineSegment(sketch, "E336", {"start": v(-473.78, -122.87) * mm, "end": v(-488.75, -140.3) * mm});
            skArc(sketch, "E337", {"start": v(-488.75, -140.3) * mm, "mid": v(-482.6, -176.43) * mm, "end": v(-448.22, -163.7) * mm});
            skLineSegment(sketch, "E338", {"start": v(-448.22, -163.7) * mm, "end": v(-440.62, -142.01) * mm});
            skArc(sketch, "E339", {"start": v(-440.62, -142.01) * mm, "mid": v(-449.26, -118.7) * mm, "end": v(-473.78, -122.87) * mm});
            skLineSegment(sketch, "E340", {"start": v(-425.55, -146.05) * mm, "end": v(-429.8, -168.63) * mm});
            skArc(sketch, "E341", {"start": v(-429.8, -168.63) * mm, "mid": v(-406.4, -196.85) * mm, "end": v(-383, -168.63) * mm});
            skLineSegment(sketch, "E342", {"start": v(-383, -168.63) * mm, "end": v(-387.25, -146.05) * mm});
            skArc(sketch, "E343", {"start": v(-387.25, -146.05) * mm, "mid": v(-406.4, -130.18) * mm, "end": v(-425.55, -146.05) * mm});
            skLineSegment(sketch, "E344", {"start": v(-372.18, -142.01) * mm, "end": v(-364.58, -163.7) * mm});
            skArc(sketch, "E345", {"start": v(-364.58, -163.7) * mm, "mid": v(-330.2, -176.43) * mm, "end": v(-324.05, -140.3) * mm});
            skLineSegment(sketch, "E346", {"start": v(-324.05, -140.3) * mm, "end": v(-339.02, -122.87) * mm});
            skArc(sketch, "E347", {"start": v(-339.02, -122.87) * mm, "mid": v(-363.54, -118.7) * mm, "end": v(-372.18, -142.01) * mm});
            skLineSegment(sketch, "E348", {"start": v(-327.98, -111.83) * mm, "end": v(-310.56, -126.8) * mm});
            skArc(sketch, "E349", {"start": v(-310.56, -126.8) * mm, "mid": v(-274.42, -120.65) * mm, "end": v(-287.16, -86.27) * mm});
            skLineSegment(sketch, "E350", {"start": v(-287.16, -86.27) * mm, "end": v(-308.84, -78.67) * mm});
            skArc(sketch, "E351", {"start": v(-308.84, -78.67) * mm, "mid": v(-332.16, -87.31) * mm, "end": v(-327.98, -111.83) * mm});
            skLineSegment(sketch, "E352", {"start": v(-304.8, -63.6) * mm, "end": v(-282.22, -67.85) * mm});
            skArc(sketch, "E353", {"start": v(-282.22, -67.85) * mm, "mid": v(-254, -44.45) * mm, "end": v(-282.22, -21.05) * mm});
            skLineSegment(sketch, "E354", {"start": v(-282.22, -21.05) * mm, "end": v(-304.8, -25.3) * mm});
            skArc(sketch, "E355", {"start": v(-304.8, -25.3) * mm, "mid": v(-320.68, -44.45) * mm, "end": v(-304.8, -63.6) * mm});
            skLineSegment(sketch, "E356", {"start": v(-308.84, -10.23) * mm, "end": v(-287.16, -2.63) * mm});
            skArc(sketch, "E357", {"start": v(-287.16, -2.63) * mm, "mid": v(-274.42, 31.75) * mm, "end": v(-310.56, 37.9) * mm});
            skLineSegment(sketch, "E358", {"start": v(-310.56, 37.9) * mm, "end": v(-327.98, 22.93) * mm});
            skArc(sketch, "E359", {"start": v(-327.98, 22.93) * mm, "mid": v(-332.16, -1.59) * mm, "end": v(-308.84, -10.23) * mm});
            skLineSegment(sketch, "E360", {"start": v(-339.02, 33.97) * mm, "end": v(-324.05, 51.4) * mm});
            skArc(sketch, "E361", {"start": v(-324.05, 51.4) * mm, "mid": v(-330.2, 87.53) * mm, "end": v(-364.58, 74.8) * mm});
            skLineSegment(sketch, "E362", {"start": v(-364.58, 74.8) * mm, "end": v(-372.18, 53.11) * mm});
            skArc(sketch, "E363", {"start": v(-372.18, 53.11) * mm, "mid": v(-363.54, 29.8) * mm, "end": v(-339.02, 33.97) * mm});
            skCircle(sketch, "E364", {"center": v(-445.73, 102.31) * mm, "radius": 7.94 * mm});
            skCircle(sketch, "E365", {"center": v(-513.84, 62.99) * mm, "radius": 7.94 * mm});
            skCircle(sketch, "E366", {"center": v(-553.16, -5.12) * mm, "radius": 7.94 * mm});
            skCircle(sketch, "E367", {"center": v(-553.16, -83.78) * mm, "radius": 7.94 * mm});
            skCircle(sketch, "E368", {"center": v(-513.84, -151.89) * mm, "radius": 7.94 * mm});
            skCircle(sketch, "E369", {"center": v(-445.73, -191.21) * mm, "radius": 7.94 * mm});
            skCircle(sketch, "E370", {"center": v(-367.07, -191.21) * mm, "radius": 7.94 * mm});
            skCircle(sketch, "E371", {"center": v(-298.96, -151.89) * mm, "radius": 7.94 * mm});
            skCircle(sketch, "E372", {"center": v(-259.64, -83.78) * mm, "radius": 7.94 * mm});
            skCircle(sketch, "E373", {"center": v(-259.64, -5.12) * mm, "radius": 7.94 * mm});
            skCircle(sketch, "E374", {"center": v(-298.96, 62.99) * mm, "radius": 7.94 * mm});
            skCircle(sketch, "E375", {"center": v(-367.07, 102.31) * mm, "radius": 7.94 * mm});
            skCircle(sketch, "E376", {"center": v(-44.45, 317.5) * mm, "radius": 171.45 * mm});
            skCircle(sketch, "E377", {"center": v(-44.45, 317.5) * mm, "radius": 69.85 * mm});
            skLineSegment(sketch, "E378", {"start": v(-25.3, 419.1) * mm, "end": v(-21.05, 441.68) * mm});
            skArc(sketch, "E379", {"start": v(-21.05, 441.68) * mm, "mid": v(-44.45, 469.9) * mm, "end": v(-67.85, 441.68) * mm});
            skLineSegment(sketch, "E380", {"start": v(-67.85, 441.68) * mm, "end": v(-63.6, 419.1) * mm});
            skArc(sketch, "E381", {"start": v(-63.6, 419.1) * mm, "mid": v(-44.45, 403.23) * mm, "end": v(-25.3, 419.1) * mm});
            skLineSegment(sketch, "E382", {"start": v(-78.67, 415.06) * mm, "end": v(-86.27, 436.74) * mm});
            skArc(sketch, "E383", {"start": v(-86.27, 436.74) * mm, "mid": v(-120.65, 449.48) * mm, "end": v(-126.8, 413.34) * mm});
            skLineSegment(sketch, "E384", {"start": v(-126.8, 413.34) * mm, "end": v(-111.83, 395.92) * mm});
            skArc(sketch, "E385", {"start": v(-111.83, 395.92) * mm, "mid": v(-87.31, 391.74) * mm, "end": v(-78.67, 415.06) * mm});
            skLineSegment(sketch, "E386", {"start": v(-122.87, 384.88) * mm, "end": v(-140.3, 399.85) * mm});
            skArc(sketch, "E387", {"start": v(-140.3, 399.85) * mm, "mid": v(-176.43, 393.7) * mm, "end": v(-163.7, 359.32) * mm});
            skLineSegment(sketch, "E388", {"start": v(-163.7, 359.32) * mm, "end": v(-142.01, 351.72) * mm});
            skArc(sketch, "E389", {"start": v(-142.01, 351.72) * mm, "mid": v(-118.7, 360.36) * mm, "end": v(-122.87, 384.88) * mm});
            skLineSegment(sketch, "E390", {"start": v(-146.05, 336.65) * mm, "end": v(-168.63, 340.9) * mm});
            skArc(sketch, "E391", {"start": v(-168.63, 340.9) * mm, "mid": v(-196.85, 317.5) * mm, "end": v(-168.63, 294.1) * mm});
            skLineSegment(sketch, "E392", {"start": v(-168.63, 294.1) * mm, "end": v(-146.05, 298.35) * mm});
            skArc(sketch, "E393", {"start": v(-146.05, 298.35) * mm, "mid": v(-130.18, 317.5) * mm, "end": v(-146.05, 336.65) * mm});
            skLineSegment(sketch, "E394", {"start": v(-142.01, 283.28) * mm, "end": v(-163.7, 275.68) * mm});
            skArc(sketch, "E395", {"start": v(-163.7, 275.68) * mm, "mid": v(-176.43, 241.3) * mm, "end": v(-140.3, 235.15) * mm});
            skLineSegment(sketch, "E396", {"start": v(-140.3, 235.15) * mm, "end": v(-122.87, 250.12) * mm});
            skArc(sketch, "E397", {"start": v(-122.87, 250.12) * mm, "mid": v(-118.7, 274.64) * mm, "end": v(-142.01, 283.28) * mm});
            skLineSegment(sketch, "E398", {"start": v(-111.83, 239.08) * mm, "end": v(-126.8, 221.66) * mm});
            skArc(sketch, "E399", {"start": v(-126.8, 221.66) * mm, "mid": v(-120.65, 185.52) * mm, "end": v(-86.27, 198.26) * mm});
            skLineSegment(sketch, "E400", {"start": v(-86.27, 198.26) * mm, "end": v(-78.67, 219.94) * mm});
            skArc(sketch, "E401", {"start": v(-78.67, 219.94) * mm, "mid": v(-87.31, 243.26) * mm, "end": v(-111.83, 239.08) * mm});
            skLineSegment(sketch, "E402", {"start": v(-63.6, 215.9) * mm, "end": v(-67.85, 193.32) * mm});
            skArc(sketch, "E403", {"start": v(-67.85, 193.32) * mm, "mid": v(-44.45, 165.1) * mm, "end": v(-21.05, 193.32) * mm});
            skLineSegment(sketch, "E404", {"start": v(-21.05, 193.32) * mm, "end": v(-25.3, 215.9) * mm});
            skArc(sketch, "E405", {"start": v(-25.3, 215.9) * mm, "mid": v(-44.45, 231.77) * mm, "end": v(-63.6, 215.9) * mm});
            skLineSegment(sketch, "E406", {"start": v(-10.23, 219.94) * mm, "end": v(-2.63, 198.26) * mm});
            skArc(sketch, "E407", {"start": v(-2.63, 198.26) * mm, "mid": v(31.75, 185.52) * mm, "end": v(37.9, 221.66) * mm});
            skLineSegment(sketch, "E408", {"start": v(37.9, 221.66) * mm, "end": v(22.93, 239.08) * mm});
            skArc(sketch, "E409", {"start": v(22.93, 239.08) * mm, "mid": v(-1.59, 243.26) * mm, "end": v(-10.23, 219.94) * mm});
            skLineSegment(sketch, "E410", {"start": v(33.97, 250.12) * mm, "end": v(51.4, 235.15) * mm});
            skArc(sketch, "E411", {"start": v(51.4, 235.15) * mm, "mid": v(87.53, 241.3) * mm, "end": v(74.8, 275.68) * mm});
            skLineSegment(sketch, "E412", {"start": v(74.8, 275.68) * mm, "end": v(53.11, 283.28) * mm});
            skArc(sketch, "E413", {"start": v(53.11, 283.28) * mm, "mid": v(29.8, 274.64) * mm, "end": v(33.97, 250.12) * mm});
            skLineSegment(sketch, "E414", {"start": v(57.15, 298.35) * mm, "end": v(79.73, 294.1) * mm});
            skArc(sketch, "E415", {"start": v(79.73, 294.1) * mm, "mid": v(107.95, 317.5) * mm, "end": v(79.73, 340.9) * mm});
            skLineSegment(sketch, "E416", {"start": v(79.73, 340.9) * mm, "end": v(57.15, 336.65) * mm});
            skArc(sketch, "E417", {"start": v(57.15, 336.65) * mm, "mid": v(41.27, 317.5) * mm, "end": v(57.15, 298.35) * mm});
            skLineSegment(sketch, "E418", {"start": v(53.11, 351.72) * mm, "end": v(74.8, 359.32) * mm});
            skArc(sketch, "E419", {"start": v(74.8, 359.32) * mm, "mid": v(87.53, 393.7) * mm, "end": v(51.4, 399.85) * mm});
            skLineSegment(sketch, "E420", {"start": v(51.4, 399.85) * mm, "end": v(33.97, 384.88) * mm});
            skArc(sketch, "E421", {"start": v(33.97, 384.88) * mm, "mid": v(29.8, 360.36) * mm, "end": v(53.11, 351.72) * mm});
            skLineSegment(sketch, "E422", {"start": v(22.93, 395.92) * mm, "end": v(37.9, 413.34) * mm});
            skArc(sketch, "E423", {"start": v(37.9, 413.34) * mm, "mid": v(31.75, 449.48) * mm, "end": v(-2.63, 436.74) * mm});
            skLineSegment(sketch, "E424", {"start": v(-2.63, 436.74) * mm, "end": v(-10.23, 415.06) * mm});
            skArc(sketch, "E425", {"start": v(-10.23, 415.06) * mm, "mid": v(-1.59, 391.74) * mm, "end": v(22.93, 395.92) * mm});
            skCircle(sketch, "E426", {"center": v(-83.78, 464.26) * mm, "radius": 7.94 * mm});
            skCircle(sketch, "E427", {"center": v(-151.89, 424.94) * mm, "radius": 7.94 * mm});
            skCircle(sketch, "E428", {"center": v(-191.21, 356.83) * mm, "radius": 7.94 * mm});
            skCircle(sketch, "E429", {"center": v(-191.21, 278.17) * mm, "radius": 7.94 * mm});
            skCircle(sketch, "E430", {"center": v(-151.89, 210.06) * mm, "radius": 7.94 * mm});
            skCircle(sketch, "E431", {"center": v(-83.78, 170.74) * mm, "radius": 7.94 * mm});
            skCircle(sketch, "E432", {"center": v(-5.12, 170.74) * mm, "radius": 7.94 * mm});
            skCircle(sketch, "E433", {"center": v(62.99, 210.06) * mm, "radius": 7.94 * mm});
            skCircle(sketch, "E434", {"center": v(102.31, 278.17) * mm, "radius": 7.94 * mm});
            skCircle(sketch, "E435", {"center": v(102.31, 356.83) * mm, "radius": 7.94 * mm});
            skCircle(sketch, "E436", {"center": v(62.99, 424.94) * mm, "radius": 7.94 * mm});
            skCircle(sketch, "E437", {"center": v(-5.12, 464.26) * mm, "radius": 7.94 * mm});
            skCircle(sketch, "E438", {"center": v(-406.4, 317.5) * mm, "radius": 171.45 * mm});
            skCircle(sketch, "E439", {"center": v(-406.4, 317.5) * mm, "radius": 69.85 * mm});
            skLineSegment(sketch, "E440", {"start": v(-387.25, 419.1) * mm, "end": v(-383, 441.68) * mm});
            skArc(sketch, "E441", {"start": v(-383, 441.68) * mm, "mid": v(-406.4, 469.9) * mm, "end": v(-429.8, 441.68) * mm});
            skLineSegment(sketch, "E442", {"start": v(-429.8, 441.68) * mm, "end": v(-425.55, 419.1) * mm});
            skArc(sketch, "E443", {"start": v(-425.55, 419.1) * mm, "mid": v(-406.4, 403.23) * mm, "end": v(-387.25, 419.1) * mm});
            skLineSegment(sketch, "E444", {"start": v(-440.62, 415.06) * mm, "end": v(-448.22, 436.74) * mm});
            skArc(sketch, "E445", {"start": v(-448.22, 436.74) * mm, "mid": v(-482.6, 449.48) * mm, "end": v(-488.75, 413.34) * mm});
            skLineSegment(sketch, "E446", {"start": v(-488.75, 413.34) * mm, "end": v(-473.78, 395.92) * mm});
            skArc(sketch, "E447", {"start": v(-473.78, 395.92) * mm, "mid": v(-449.26, 391.74) * mm, "end": v(-440.62, 415.06) * mm});
            skLineSegment(sketch, "E448", {"start": v(-484.82, 384.88) * mm, "end": v(-502.24, 399.85) * mm});
            skArc(sketch, "E449", {"start": v(-502.24, 399.85) * mm, "mid": v(-538.38, 393.7) * mm, "end": v(-525.64, 359.32) * mm});
            skLineSegment(sketch, "E450", {"start": v(-525.64, 359.32) * mm, "end": v(-503.96, 351.72) * mm});
            skArc(sketch, "E451", {"start": v(-503.96, 351.72) * mm, "mid": v(-480.64, 360.36) * mm, "end": v(-484.82, 384.88) * mm});
            skLineSegment(sketch, "E452", {"start": v(-508, 336.65) * mm, "end": v(-530.58, 340.9) * mm});
            skArc(sketch, "E453", {"start": v(-530.58, 340.9) * mm, "mid": v(-558.8, 317.5) * mm, "end": v(-530.58, 294.1) * mm});
            skLineSegment(sketch, "E454", {"start": v(-530.58, 294.1) * mm, "end": v(-508, 298.35) * mm});
            skArc(sketch, "E455", {"start": v(-508, 298.35) * mm, "mid": v(-492.13, 317.5) * mm, "end": v(-508, 336.65) * mm});
            skLineSegment(sketch, "E456", {"start": v(-503.96, 283.28) * mm, "end": v(-525.64, 275.68) * mm});
            skArc(sketch, "E457", {"start": v(-525.64, 275.68) * mm, "mid": v(-538.38, 241.3) * mm, "end": v(-502.24, 235.15) * mm});
            skLineSegment(sketch, "E458", {"start": v(-502.24, 235.15) * mm, "end": v(-484.82, 250.12) * mm});
            skArc(sketch, "E459", {"start": v(-484.82, 250.12) * mm, "mid": v(-480.64, 274.64) * mm, "end": v(-503.96, 283.28) * mm});
            skLineSegment(sketch, "E460", {"start": v(-473.78, 239.08) * mm, "end": v(-488.75, 221.66) * mm});
            skArc(sketch, "E461", {"start": v(-488.75, 221.66) * mm, "mid": v(-482.6, 185.52) * mm, "end": v(-448.22, 198.26) * mm});
            skLineSegment(sketch, "E462", {"start": v(-448.22, 198.26) * mm, "end": v(-440.62, 219.94) * mm});
            skArc(sketch, "E463", {"start": v(-440.62, 219.94) * mm, "mid": v(-449.26, 243.26) * mm, "end": v(-473.78, 239.08) * mm});
            skLineSegment(sketch, "E464", {"start": v(-425.55, 215.9) * mm, "end": v(-429.8, 193.32) * mm});
            skArc(sketch, "E465", {"start": v(-429.8, 193.32) * mm, "mid": v(-406.4, 165.1) * mm, "end": v(-383, 193.32) * mm});
            skLineSegment(sketch, "E466", {"start": v(-383, 193.32) * mm, "end": v(-387.25, 215.9) * mm});
            skArc(sketch, "E467", {"start": v(-387.25, 215.9) * mm, "mid": v(-406.4, 231.77) * mm, "end": v(-425.55, 215.9) * mm});
            skLineSegment(sketch, "E468", {"start": v(-372.18, 219.94) * mm, "end": v(-364.58, 198.26) * mm});
            skArc(sketch, "E469", {"start": v(-364.58, 198.26) * mm, "mid": v(-330.2, 185.52) * mm, "end": v(-324.05, 221.66) * mm});
            skLineSegment(sketch, "E470", {"start": v(-324.05, 221.66) * mm, "end": v(-339.02, 239.08) * mm});
            skArc(sketch, "E471", {"start": v(-339.02, 239.08) * mm, "mid": v(-363.54, 243.26) * mm, "end": v(-372.18, 219.94) * mm});
            skLineSegment(sketch, "E472", {"start": v(-327.98, 250.12) * mm, "end": v(-310.56, 235.15) * mm});
            skArc(sketch, "E473", {"start": v(-310.56, 235.15) * mm, "mid": v(-274.42, 241.3) * mm, "end": v(-287.16, 275.68) * mm});
            skLineSegment(sketch, "E474", {"start": v(-287.16, 275.68) * mm, "end": v(-308.84, 283.28) * mm});
            skArc(sketch, "E475", {"start": v(-308.84, 283.28) * mm, "mid": v(-332.16, 274.64) * mm, "end": v(-327.98, 250.12) * mm});
            skLineSegment(sketch, "E476", {"start": v(-304.8, 298.35) * mm, "end": v(-282.22, 294.1) * mm});
            skArc(sketch, "E477", {"start": v(-282.22, 294.1) * mm, "mid": v(-254, 317.5) * mm, "end": v(-282.22, 340.9) * mm});
            skLineSegment(sketch, "E478", {"start": v(-282.22, 340.9) * mm, "end": v(-304.8, 336.65) * mm});
            skArc(sketch, "E479", {"start": v(-304.8, 336.65) * mm, "mid": v(-320.68, 317.5) * mm, "end": v(-304.8, 298.35) * mm});
            skLineSegment(sketch, "E480", {"start": v(-308.84, 351.72) * mm, "end": v(-287.16, 359.32) * mm});
            skArc(sketch, "E481", {"start": v(-287.16, 359.32) * mm, "mid": v(-274.42, 393.7) * mm, "end": v(-310.56, 399.85) * mm});
            skLineSegment(sketch, "E482", {"start": v(-310.56, 399.85) * mm, "end": v(-327.98, 384.88) * mm});
            skArc(sketch, "E483", {"start": v(-327.98, 384.88) * mm, "mid": v(-332.16, 360.36) * mm, "end": v(-308.84, 351.72) * mm});
            skLineSegment(sketch, "E484", {"start": v(-339.02, 395.92) * mm, "end": v(-324.05, 413.34) * mm});
            skArc(sketch, "E485", {"start": v(-324.05, 413.34) * mm, "mid": v(-330.2, 449.48) * mm, "end": v(-364.58, 436.74) * mm});
            skLineSegment(sketch, "E486", {"start": v(-364.58, 436.74) * mm, "end": v(-372.18, 415.06) * mm});
            skArc(sketch, "E487", {"start": v(-372.18, 415.06) * mm, "mid": v(-363.54, 391.74) * mm, "end": v(-339.02, 395.92) * mm});
            skCircle(sketch, "E488", {"center": v(-445.73, 464.26) * mm, "radius": 7.94 * mm});
            skCircle(sketch, "E489", {"center": v(-513.84, 424.94) * mm, "radius": 7.94 * mm});
            skCircle(sketch, "E490", {"center": v(-553.16, 356.83) * mm, "radius": 7.94 * mm});
            skCircle(sketch, "E491", {"center": v(-553.16, 278.17) * mm, "radius": 7.94 * mm});
            skCircle(sketch, "E492", {"center": v(-513.84, 210.06) * mm, "radius": 7.94 * mm});
            skCircle(sketch, "E493", {"center": v(-445.73, 170.74) * mm, "radius": 7.94 * mm});
            skCircle(sketch, "E494", {"center": v(-367.07, 170.74) * mm, "radius": 7.94 * mm});
            skCircle(sketch, "E495", {"center": v(-298.96, 210.06) * mm, "radius": 7.94 * mm});
            skCircle(sketch, "E496", {"center": v(-259.64, 278.17) * mm, "radius": 7.94 * mm});
            skCircle(sketch, "E497", {"center": v(-259.64, 356.83) * mm, "radius": 7.94 * mm});
            skCircle(sketch, "E498", {"center": v(-298.96, 424.94) * mm, "radius": 7.94 * mm});
            skCircle(sketch, "E499", {"center": v(-367.07, 464.26) * mm, "radius": 7.94 * mm});
            skCircle(sketch, "E500", {"center": v(317.5, 317.5) * mm, "radius": 171.45 * mm});
            skCircle(sketch, "E501", {"center": v(317.5, 317.5) * mm, "radius": 69.85 * mm});
            skLineSegment(sketch, "E502", {"start": v(336.65, 419.1) * mm, "end": v(340.9, 441.68) * mm});
            skArc(sketch, "E503", {"start": v(340.9, 441.68) * mm, "mid": v(317.5, 469.9) * mm, "end": v(294.1, 441.68) * mm});
            skLineSegment(sketch, "E504", {"start": v(294.1, 441.68) * mm, "end": v(298.35, 419.1) * mm});
            skArc(sketch, "E505", {"start": v(298.35, 419.1) * mm, "mid": v(317.5, 403.23) * mm, "end": v(336.65, 419.1) * mm});
            skLineSegment(sketch, "E506", {"start": v(283.28, 415.06) * mm, "end": v(275.68, 436.74) * mm});
            skArc(sketch, "E507", {"start": v(275.68, 436.74) * mm, "mid": v(241.3, 449.48) * mm, "end": v(235.15, 413.34) * mm});
            skLineSegment(sketch, "E508", {"start": v(235.15, 413.34) * mm, "end": v(250.12, 395.92) * mm});
            skArc(sketch, "E509", {"start": v(250.12, 395.92) * mm, "mid": v(274.64, 391.74) * mm, "end": v(283.28, 415.06) * mm});
            skLineSegment(sketch, "E510", {"start": v(239.08, 384.88) * mm, "end": v(221.66, 399.85) * mm});
            skArc(sketch, "E511", {"start": v(221.66, 399.85) * mm, "mid": v(185.52, 393.7) * mm, "end": v(198.26, 359.32) * mm});
            skLineSegment(sketch, "E512", {"start": v(198.26, 359.32) * mm, "end": v(219.94, 351.72) * mm});
            skArc(sketch, "E513", {"start": v(219.94, 351.72) * mm, "mid": v(243.26, 360.36) * mm, "end": v(239.08, 384.88) * mm});
            skLineSegment(sketch, "E514", {"start": v(215.9, 336.65) * mm, "end": v(193.32, 340.9) * mm});
            skArc(sketch, "E515", {"start": v(193.32, 340.9) * mm, "mid": v(165.1, 317.5) * mm, "end": v(193.32, 294.1) * mm});
            skLineSegment(sketch, "E516", {"start": v(193.32, 294.1) * mm, "end": v(215.9, 298.35) * mm});
            skArc(sketch, "E517", {"start": v(215.9, 298.35) * mm, "mid": v(231.77, 317.5) * mm, "end": v(215.9, 336.65) * mm});
            skLineSegment(sketch, "E518", {"start": v(219.94, 283.28) * mm, "end": v(198.26, 275.68) * mm});
            skArc(sketch, "E519", {"start": v(198.26, 275.68) * mm, "mid": v(185.52, 241.3) * mm, "end": v(221.66, 235.15) * mm});
            skLineSegment(sketch, "E520", {"start": v(221.66, 235.15) * mm, "end": v(239.08, 250.12) * mm});
            skArc(sketch, "E521", {"start": v(239.08, 250.12) * mm, "mid": v(243.26, 274.64) * mm, "end": v(219.94, 283.28) * mm});
            skLineSegment(sketch, "E522", {"start": v(250.12, 239.08) * mm, "end": v(235.15, 221.66) * mm});
            skArc(sketch, "E523", {"start": v(235.15, 221.66) * mm, "mid": v(241.3, 185.52) * mm, "end": v(275.68, 198.26) * mm});
            skLineSegment(sketch, "E524", {"start": v(275.68, 198.26) * mm, "end": v(283.28, 219.94) * mm});
            skArc(sketch, "E525", {"start": v(283.28, 219.94) * mm, "mid": v(274.64, 243.26) * mm, "end": v(250.12, 239.08) * mm});
            skLineSegment(sketch, "E526", {"start": v(298.35, 215.9) * mm, "end": v(294.1, 193.32) * mm});
            skArc(sketch, "E527", {"start": v(294.1, 193.32) * mm, "mid": v(317.5, 165.1) * mm, "end": v(340.9, 193.32) * mm});
            skLineSegment(sketch, "E528", {"start": v(340.9, 193.32) * mm, "end": v(336.65, 215.9) * mm});
            skArc(sketch, "E529", {"start": v(336.65, 215.9) * mm, "mid": v(317.5, 231.77) * mm, "end": v(298.35, 215.9) * mm});
            skLineSegment(sketch, "E530", {"start": v(351.72, 219.94) * mm, "end": v(359.32, 198.26) * mm});
            skArc(sketch, "E531", {"start": v(359.32, 198.26) * mm, "mid": v(393.7, 185.52) * mm, "end": v(399.85, 221.66) * mm});
            skLineSegment(sketch, "E532", {"start": v(399.85, 221.66) * mm, "end": v(384.88, 239.08) * mm});
            skArc(sketch, "E533", {"start": v(384.88, 239.08) * mm, "mid": v(360.36, 243.26) * mm, "end": v(351.72, 219.94) * mm});
            skLineSegment(sketch, "E534", {"start": v(395.92, 250.12) * mm, "end": v(413.34, 235.15) * mm});
            skArc(sketch, "E535", {"start": v(413.34, 235.15) * mm, "mid": v(449.48, 241.3) * mm, "end": v(436.74, 275.68) * mm});
            skLineSegment(sketch, "E536", {"start": v(436.74, 275.68) * mm, "end": v(415.06, 283.28) * mm});
            skArc(sketch, "E537", {"start": v(415.06, 283.28) * mm, "mid": v(391.74, 274.64) * mm, "end": v(395.92, 250.12) * mm});
            skLineSegment(sketch, "E538", {"start": v(419.1, 298.35) * mm, "end": v(441.68, 294.1) * mm});
            skArc(sketch, "E539", {"start": v(441.68, 294.1) * mm, "mid": v(469.9, 317.5) * mm, "end": v(441.68, 340.9) * mm});
            skLineSegment(sketch, "E540", {"start": v(441.68, 340.9) * mm, "end": v(419.1, 336.65) * mm});
            skArc(sketch, "E541", {"start": v(419.1, 336.65) * mm, "mid": v(403.23, 317.5) * mm, "end": v(419.1, 298.35) * mm});
            skLineSegment(sketch, "E542", {"start": v(415.06, 351.72) * mm, "end": v(436.74, 359.32) * mm});
            skArc(sketch, "E543", {"start": v(436.74, 359.32) * mm, "mid": v(449.48, 393.7) * mm, "end": v(413.34, 399.85) * mm});
            skLineSegment(sketch, "E544", {"start": v(413.34, 399.85) * mm, "end": v(395.92, 384.88) * mm});
            skArc(sketch, "E545", {"start": v(395.92, 384.88) * mm, "mid": v(391.74, 360.36) * mm, "end": v(415.06, 351.72) * mm});
            skLineSegment(sketch, "E546", {"start": v(384.88, 395.92) * mm, "end": v(399.85, 413.34) * mm});
            skArc(sketch, "E547", {"start": v(399.85, 413.34) * mm, "mid": v(393.7, 449.48) * mm, "end": v(359.32, 436.74) * mm});
            skLineSegment(sketch, "E548", {"start": v(359.32, 436.74) * mm, "end": v(351.72, 415.06) * mm});
            skArc(sketch, "E549", {"start": v(351.72, 415.06) * mm, "mid": v(360.36, 391.74) * mm, "end": v(384.88, 395.92) * mm});
            skCircle(sketch, "E550", {"center": v(278.17, 464.26) * mm, "radius": 7.94 * mm});
            skCircle(sketch, "E551", {"center": v(210.06, 424.94) * mm, "radius": 7.94 * mm});
            skCircle(sketch, "E552", {"center": v(170.74, 356.83) * mm, "radius": 7.94 * mm});
            skCircle(sketch, "E553", {"center": v(170.74, 278.17) * mm, "radius": 7.94 * mm});
            skCircle(sketch, "E554", {"center": v(210.06, 210.06) * mm, "radius": 7.94 * mm});
            skCircle(sketch, "E555", {"center": v(278.17, 170.74) * mm, "radius": 7.94 * mm});
            skCircle(sketch, "E556", {"center": v(356.83, 170.74) * mm, "radius": 7.94 * mm});
            skCircle(sketch, "E557", {"center": v(424.94, 210.06) * mm, "radius": 7.94 * mm});
            skCircle(sketch, "E558", {"center": v(464.26, 278.17) * mm, "radius": 7.94 * mm});
            skCircle(sketch, "E559", {"center": v(464.26, 356.83) * mm, "radius": 7.94 * mm});
            skCircle(sketch, "E560", {"center": v(424.94, 424.94) * mm, "radius": 7.94 * mm});
            skCircle(sketch, "E561", {"center": v(356.83, 464.26) * mm, "radius": 7.94 * mm});
            skSolve(sketch);
        }
        {
            var Q0;
            Q0=makeQuery(id+"F0.imprint","IMPRINT",FACE,{"disambiguationData":[TD([[makeQuery(id+"F0.imprint","IMPRINT",EDGE,{"derivedFrom":sQuery(id+"F0.wireOp",EDGE,"E438")}),-1.0]])]});
            extrude(context, id + "F1", {"entities" : qUnion([Q0]), "depth" : 25.4 * mm});
        }
    });
